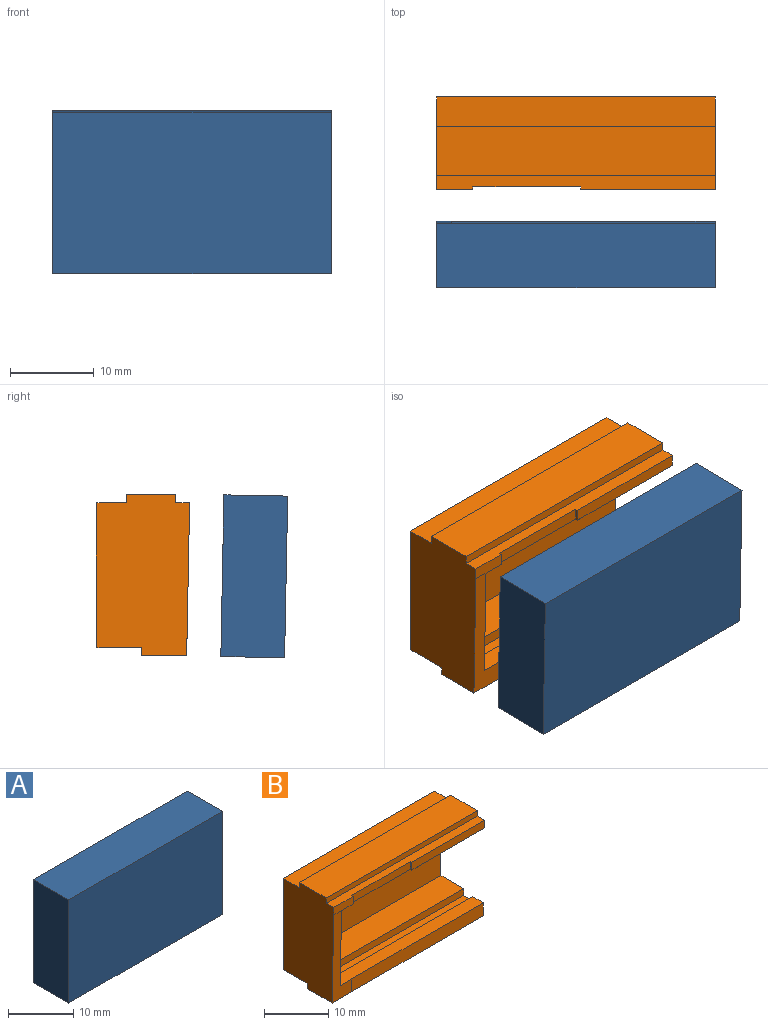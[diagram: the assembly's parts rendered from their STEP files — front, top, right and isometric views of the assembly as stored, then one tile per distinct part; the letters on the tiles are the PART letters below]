
ASSEMBLY  parts=2 mates=1
PART A: 18 faces, bbox 33.2x7.6x19.3 mm
  f0: plane 19.32x7.62mm, normal (-1,0,0), area 147.2mm2, adj f1,f7,f10,f16
  f1: plane 33.23x7.62mm, normal (0,0,1), area 253.2mm2, adj f0,f3,f7,f16
  f2: plane 31.52x1.89mm, normal (0,0,-1), area 59.4mm2, adj f3,f6,f11,f15
  f3: plane 19.32x7.62mm, normal (1,0,0), area 53.3mm2, adj f1,f2,f4,f5,f7,f8,f9,f10
  f4: plane 31.52x2.4mm, normal (0,0,-1), area 75.6mm2, adj f3,f6,f7,f14
  f5: plane 31.52x2.4mm, normal (0,0,1), area 75.6mm2, adj f3,f6,f7,f13
  f6: plane 16.1x6.29mm, normal (1,0,0), area 94mm2, adj f2,f4,f5,f7,f8,f9,f11,f12
  f7: plane 33.23x19.32mm, normal (0,1,0), area 187.8mm2, adj f0,f1,f3,f4,f5,f6,f10
  f8: plane 31.52x2mm, normal (0,0,-1), area 63mm2, adj f3,f6,f11,f14
  f9: plane 31.52x3.2mm, normal (0,0,1), area 100.9mm2, adj f3,f6,f12,f13
  f10: plane 33.23x7.62mm, normal (0,0,-1), area 253.2mm2, adj f0,f3,f7,f16
  f11: plane 31.52x1.29mm, normal (0,1,0), area 40.7mm2, adj f2,f3,f6,f8
  f12: plane 31.52x1.12mm, normal (0,1,0), area 35.4mm2, adj f3,f6,f9,f17
  f13: plane 31.52x0.89mm, normal (0,-1,0), area 28.1mm2, adj f3,f5,f6,f9
  f14: plane 31.52x0.79mm, normal (0,-1,0), area 24.9mm2, adj f3,f4,f6,f8
  f15: plane 31.52x13.69mm, normal (0,1,0), area 431.3mm2, adj f2,f3,f6,f17
  f16: plane 33.23x19.32mm, normal (0,-1,0), area 642.2mm2, adj f0,f1,f3,f10
  f17: plane 31.52x0.69mm, normal (0,0,1), area 21.6mm2, adj f3,f6,f12,f15
PART B: 33 faces, bbox 33.2x11.1x19.3 mm
  f0: plane 4.28x1.45mm, normal (0,-1,0), area 6.2mm2, adj f18,f25,f26,f30,f32
  f1: plane 33.23x5.89mm, normal (0,0,1), area 195.8mm2, adj f6,f7,f24,f25
  f2: plane 16.05x1.45mm, normal (0,-1,0), area 23.2mm2, adj f18,f24,f28,f30,f31
  f3: plane 33.23x3.59mm, normal (0,0,1), area 119.2mm2, adj f4,f6,f24,f25
  f4: plane 33.23x17.32mm, normal (0,1,0), area 575.7mm2, adj f3,f5,f24,f25
  f5: plane 33.23x5.41mm, normal (0,0,-1), area 179.7mm2, adj f4,f8,f24,f25
  f6: plane 33.23x1.01mm, normal (0,1,0), area 33.3mm2, adj f1,f3,f24,f25
  f7: plane 33.23x1.01mm, normal (0,-1,0), area 33.4mm2, adj f1,f18,f24,f25
  f8: plane 33.23x0.99mm, normal (0,1,0), area 33mm2, adj f5,f19,f24,f25
  f9: plane 31.52x0.89mm, normal (0,1,0), area 28.1mm2, adj f10,f20,f24,f30
  f10: plane 31.52x3.2mm, normal (0,0,-1), area 100.9mm2, adj f9,f11,f20,f24
  f11: plane 31.52x1.89mm, normal (0,-1,0), area 59.6mm2, adj f10,f12,f20,f24
  f12: plane 31.52x3.77mm, normal (0,0,-1), area 118.7mm2, adj f11,f13,f20,f24
  f13: plane 31.52x12.92mm, normal (0,-1,0), area 407.1mm2, adj f12,f14,f20,f24
  f14: plane 31.52x4.97mm, normal (0,0,1), area 156.5mm2, adj f13,f15,f20,f24
  f15: plane 31.52x1.29mm, normal (0,-1,0), area 40.7mm2, adj f14,f16,f20,f24
  f16: plane 31.52x2mm, normal (0,0,1), area 63mm2, adj f15,f17,f20,f24
  f17: plane 31.52x0.79mm, normal (0,1,0), area 24.9mm2, adj f16,f20,f21,f24
  f18: plane 33.23x1.65mm, normal (0,0,1), area 50.6mm2, adj f0,f2,f7,f24,f25,f26,f28,f29
  f19: plane 33.23x5.39mm, normal (0,0,-1), area 179.2mm2, adj f8,f23,f24,f25,f32
  f20: plane 16.1x9.67mm, normal (1,0,0), area 135.5mm2, adj f9,f10,f11,f12,f13,f14,f15,f16
  f21: plane 31.52x2.42mm, normal (0,0,1), area 74.9mm2, adj f17,f20,f22,f23,f24,f32
  f22: plane 2.46x0.05mm, normal (1,0,0), area 0.1mm2, adj f21,f23,f32
  f23: plane 28.95x2.46mm, normal (0,-1,0), area 71.1mm2, adj f19,f21,f22,f24
  f24: plane 19.32x11.13mm, normal (1,0,0), area 66mm2, adj f1,f2,f3,f4,f5,f6,f7,f8
  f25: plane 19.32x11.13mm, normal (-1,0,0), area 201.6mm2, adj f0,f1,f3,f4,f5,f6,f7,f8
  f26: plane 1.45x0.33mm, normal (1,0,0), area 0.5mm2, adj f0,f18,f29,f30
  f27: plane 2.31x0.34mm, normal (0,0,-1), area 0.8mm2, adj f28,f30,f31
  f28: plane 1.45x0.33mm, normal (-1,0,0), area 0.5mm2, adj f2,f18,f27,f29,f31
  f29: plane 12.9x1.45mm, normal (0,-1,0), area 18.6mm2, adj f18,f26,f28,f30
  f30: plane 31.53x2.71mm, normal (0,0,-1), area 80.1mm2, adj f0,f2,f9,f20,f24,f26,f27,f29
  f31: plane 2.3x0.01mm, normal (0,-1,-0.02), area 0mm2, adj f2,f27,f28
  f32: plane 16.87x4.28mm, normal (0,-1,-0.02), area 35.3mm2, adj f0,f19,f20,f21,f22,f25
PLACE A rot(axis=(1,0,0),1.1deg) t=(-3.57,-2.55,-16.75)mm
PLACE B t=(-3.57,-6.55,-22.51)mm
MATE slider A.f7 <-> B.f32  axis (0,1,0.02) through (-12.59,-6.87,2.42)mm
